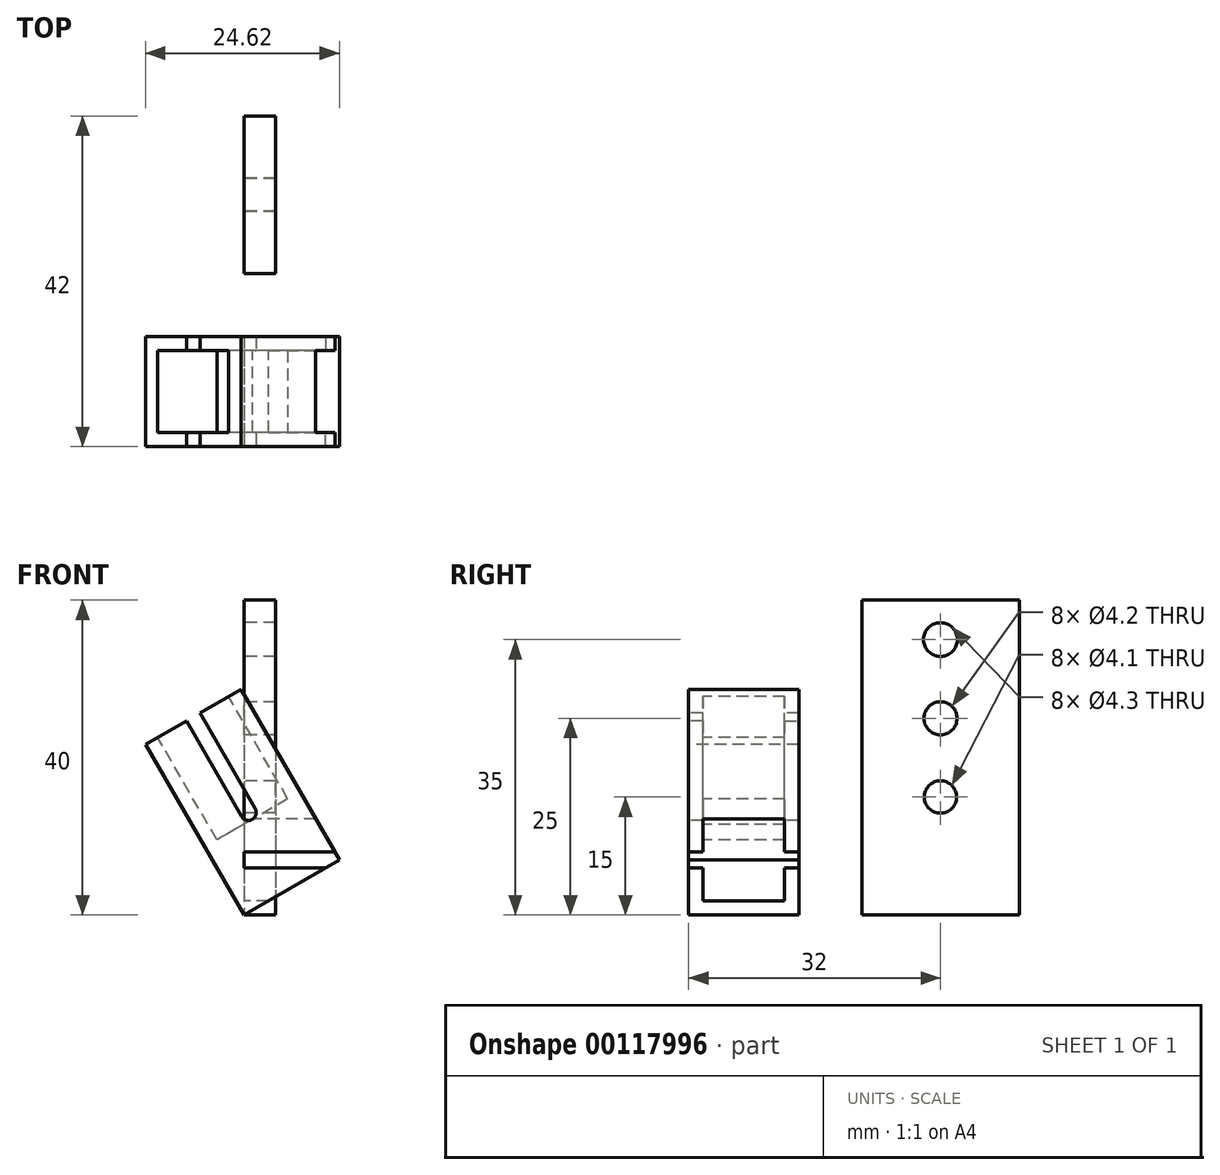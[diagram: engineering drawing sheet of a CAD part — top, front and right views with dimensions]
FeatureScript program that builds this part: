
annotation { "Feature Type Name" : "Feature", "Feature Type Description" : "" }
export const myFeature = defineFeature(function(context is Context, id is Id, definition is map)
    precondition{}
    {
        {
            var Q0;
            Q0=qCreatedBy(makeId("Right.planeOp"),FACE);
            var sketch = newSketch(context, id + "F0", { "sketchPlane" : qUnion([Q0])});
            skLineSegment(sketch, "E0.bottom", {"start": v(7, 14) * mm, "end": v(-7, 14) * mm});
            skLineSegment(sketch, "E0.top", {"start": v(7, 0) * mm, "end": v(-7, 0) * mm});
            skLineSegment(sketch, "E0.left", {"start": v(7, 14) * mm, "end": v(7, 0) * mm});
            skLineSegment(sketch, "E0.right", {"start": v(-7, 14) * mm, "end": v(-7, 0) * mm});
            skLineSegment(sketch, "E1.bottom", {"start": v(35, 40) * mm, "end": v(15, 40) * mm});
            skLineSegment(sketch, "E1.top", {"start": v(35, 0) * mm, "end": v(15, 0) * mm});
            skLineSegment(sketch, "E1.left", {"start": v(35, 40) * mm, "end": v(35, 0) * mm});
            skLineSegment(sketch, "E1.right", {"start": v(15, 40) * mm, "end": v(15, 0) * mm});
            skLineSegment(sketch, "E2", {"start": v(25, 40) * mm, "end": v(25, 0) * mm, "construction": true});
            skCircle(sketch, "E3", {"center": v(25, 15) * mm, "radius": 2.05 * mm});
            skCircle(sketch, "E4", {"center": v(25, 25) * mm, "radius": 2.1 * mm});
            skCircle(sketch, "E5", {"center": v(25, 35) * mm, "radius": 2.15 * mm});
            skLineSegment(sketch, "E6", {"start": v(7, 7) * mm, "end": v(-7, 7) * mm, "construction": true});
            skLineSegment(sketch, "E7.bottom", {"start": v(5.2, 12.2) * mm, "end": v(-5.2, 12.2) * mm});
            skLineSegment(sketch, "E7.top", {"start": v(5.2, 1.8) * mm, "end": v(-5.2, 1.8) * mm});
            skLineSegment(sketch, "E7.left", {"start": v(5.2, 12.2) * mm, "end": v(5.2, 1.8) * mm});
            skLineSegment(sketch, "E7.right", {"start": v(-5.2, 12.2) * mm, "end": v(-5.2, 1.8) * mm});
            skLineSegment(sketch, "E8", {"start": v(0, 14) * mm, "end": v(0, 0) * mm, "construction": true});
            skLineSegment(sketch, "E9", {"start": v(7, 8) * mm, "end": v(5.2, 8) * mm});
            skPoint(sketch, "E9.endSnap0", {"position": v(5.2, 7) * mm});
            skLineSegment(sketch, "E10", {"start": v(5.2, 6) * mm, "end": v(7, 6) * mm});
            skLineSegment(sketch, "E11", {"start": v(-5.2, 8) * mm, "end": v(-7, 8) * mm});
            skLineSegment(sketch, "E12", {"start": v(-5.2, 6) * mm, "end": v(-7, 6) * mm});
            skSolve(sketch);
        }
        {
            var Q0;
            Q0=makeQuery(id+"F0.imprint","IMPRINT",FACE,{"disambiguationData":[TD([[makeQuery(id+"F0.imprint","IMPRINT",EDGE,{"derivedFrom":sQuery(id+"F0.wireOp",EDGE,"E0.bottom")}),1.0]])]});
            var Q1;
            {var subQ1=sQuery(id+"F0.wireOp",EDGE,"E0.top");Q1=makeQuery(id+"F0.imprint","IMPRINT",FACE,{"disambiguationData":[TD([[makeQuery(id+"F0.imprint","IMPRINT",EDGE,{"derivedFrom":subQ1}),-1.0]])]});}
            var Q2;
            {var subQ0=sQuery(id+"F0.wireOp",EDGE,"E9");Q2=makeQuery(id+"F0.imprint","IMPRINT",FACE,{"disambiguationData":[TD([[makeQuery(id+"F0.imprint","IMPRINT",EDGE,{"derivedFrom":subQ0}),1.0]])]});}
            var Q3;
            {var subQ3=sQuery(id+"F0.wireOp",EDGE,"E7.bottom");Q3=makeQuery(id+"F0.imprint","IMPRINT",FACE,{"disambiguationData":[TD([[makeQuery(id+"F0.imprint","IMPRINT",EDGE,{"derivedFrom":subQ3}),1.0]])]});}
            var Q4;
            {var subQ0=sQuery(id+"F0.wireOp",EDGE,"E11");Q4=makeQuery(id+"F0.imprint","IMPRINT",FACE,{"disambiguationData":[TD([[makeQuery(id+"F0.imprint","IMPRINT",EDGE,{"derivedFrom":subQ0}),1.0]])]});}
            extrude(context, id + "F1", {"entities" : qUnion([Q0, Q1, Q2, Q3, Q4]), "depth" : 25 * mm});
        }
        {
            var Q0;
            Q0=makeQuery(id+"F0.imprint","IMPRINT",FACE,{"disambiguationData":[TD([[makeQuery(id+"F0.imprint","IMPRINT",EDGE,{"derivedFrom":sQuery(id+"F0.wireOp",EDGE,"E1.bottom")}),1.0]])]});
            extrude(context, id + "F2", {"entities" : qUnion([Q0]), "depth" : 4 * mm});
        }
        {
            var Q0;
            {var subQ3=sQuery(id+"F0.wireOp",EDGE,"E7.bottom");Q0=makeQuery(id+"F0.imprint","IMPRINT",FACE,{"disambiguationData":[TD([[makeQuery(id+"F0.imprint","IMPRINT",EDGE,{"derivedFrom":subQ3}),1.0]])]});}
            var Q1;
            {var subQ0=sQuery(id+"F0.wireOp",EDGE,"E9");Q1=makeQuery(id+"F0.imprint","IMPRINT",FACE,{"disambiguationData":[TD([[makeQuery(id+"F0.imprint","IMPRINT",EDGE,{"derivedFrom":subQ0}),1.0]])]});}
            var Q2;
            {var subQ0=sQuery(id+"F0.wireOp",EDGE,"E11");Q2=makeQuery(id+"F0.imprint","IMPRINT",FACE,{"disambiguationData":[TD([[makeQuery(id+"F0.imprint","IMPRINT",EDGE,{"derivedFrom":subQ0}),1.0]])]});}
            extrude(context, id + "F3", {"entities" : qUnion([Q0, Q1, Q2]), "operationType" : NewBodyOperationType.REMOVE, "depth" : 15 * mm});
        }
        {
            var Q0;
            Q0=makeQuery(id+"F1.opExtrude","SWEPT_BODY",BODY,{"disambiguationData":[OSD([sQuery(id+"F0.wireOp",EDGE,"E0.bottom"),sQuery(id+"F0.wireOp",EDGE,"E0.top"),sQuery(id+"F0.wireOp",EDGE,"E0.left"),sQuery(id+"F0.wireOp",EDGE,"E0.right")])]});
            var Q1;
            Q1=makeQuery(id+"F1.opExtrude","CAP_EDGE",EDGE,{"disambiguationData":[OSD([sQuery(id+"F0.wireOp",EDGE,"E0.top")])],"isStart":false});
            transform(context, id + "F4", {"entities" : qUnion([Q0]), "transformType" : TransformType.ROTATION, "transformAxis" : qUnion([Q1]), "angle" : 60 * degree, "oppositeDirection" : true, "makeCopy" : false});
        }
        {
            var Q0;
            Q0=makeQuery(id+"F1.opExtrude","SWEPT_BODY",BODY,{"disambiguationData":[OSD([sQuery(id+"F0.wireOp",EDGE,"E0.bottom"),sQuery(id+"F0.wireOp",EDGE,"E0.top"),sQuery(id+"F0.wireOp",EDGE,"E0.left"),sQuery(id+"F0.wireOp",EDGE,"E0.right")])]});
            transform(context, id + "F5", {"entities" : qUnion([Q0]), "transformType" : TransformType.TRANSLATION_3D, "dx" : -25 * mm, "dy" : 0 * mm, "dz" : 0 * mm, "makeCopy" : false});
        }
        {
            var Q0;
            Q0=makeQuery(id+"F3.boolean.opBoolean","COPY",EDGE,{"derivedFrom":makeQuery(id+"F3.opExtrude","CAP_EDGE",EDGE,{"disambiguationData":[OSD([sQuery(id+"F0.wireOp",EDGE,"E11")])],"isStart":false})});
            var Q1;
            Q1=makeQuery(id+"F3.boolean.opBoolean","COPY",EDGE,{"derivedFrom":makeQuery(id+"F3.opExtrude","CAP_EDGE",EDGE,{"disambiguationData":[OSD([sQuery(id+"F0.wireOp",EDGE,"E12")])],"isStart":false})});
            var Q2;
            Q2=makeQuery(id+"F3.boolean.opBoolean","COPY",EDGE,{"derivedFrom":makeQuery(id+"F3.opExtrude","CAP_EDGE",EDGE,{"disambiguationData":[OSD([sQuery(id+"F0.wireOp",EDGE,"E9")])],"isStart":false})});
            var Q3;
            Q3=makeQuery(id+"F3.boolean.opBoolean","COPY",EDGE,{"derivedFrom":makeQuery(id+"F3.opExtrude","CAP_EDGE",EDGE,{"disambiguationData":[OSD([sQuery(id+"F0.wireOp",EDGE,"E10")])],"isStart":false})});
            fillet(context, id + "F6", {"entities" : qUnion([Q0, Q1, Q2, Q3]), "radius" : 1 * mm, "tangentPropagation" : true, "allowEdgeOverflow" : false});
        }
    });
